# Revit family: Trägerplatte, MTM 2A
name_source: partatom
category: Generic Models
revit_build: Autodesk Revit 2017 (Build: 20160225_1515(x64)
units: mm (PartAtom-declared; Revit-internal decimal feet)

## family parameters
Always vertical = Yes
Can host rebar = No
Cut with Voids When Loaded = No
Part Type = Normal
Room Calculation Point = No
Round Connector Dimension = Use Diameter
Shared = No
Work Plane-Based = No

## types (1)
- MTM 2A
    Article Type = MTM 2A
    GTIN = 4012195113089
    Height = 52 mm
    Height 1 = 12 mm  [stored 0.0393701 ft]
    Manufacturer = OBO Bettermann
    Manufacturer Art.No. = 7407780
    Material = Stainless steel, grade 304
    URL = http://www.obo-bettermann.com
    Width = 72 mm  [stored 0.23622 ft]
    Width/2 = 36 mm  [stored 0.11811 ft]

note: [stored X ft] marks values corroborated as IEEE doubles in the binary element streams (Revit-internal decimal feet)

## geometry (parser evidence)
native form markers: Sweep x1
no freeform markers — native parametric forms only
